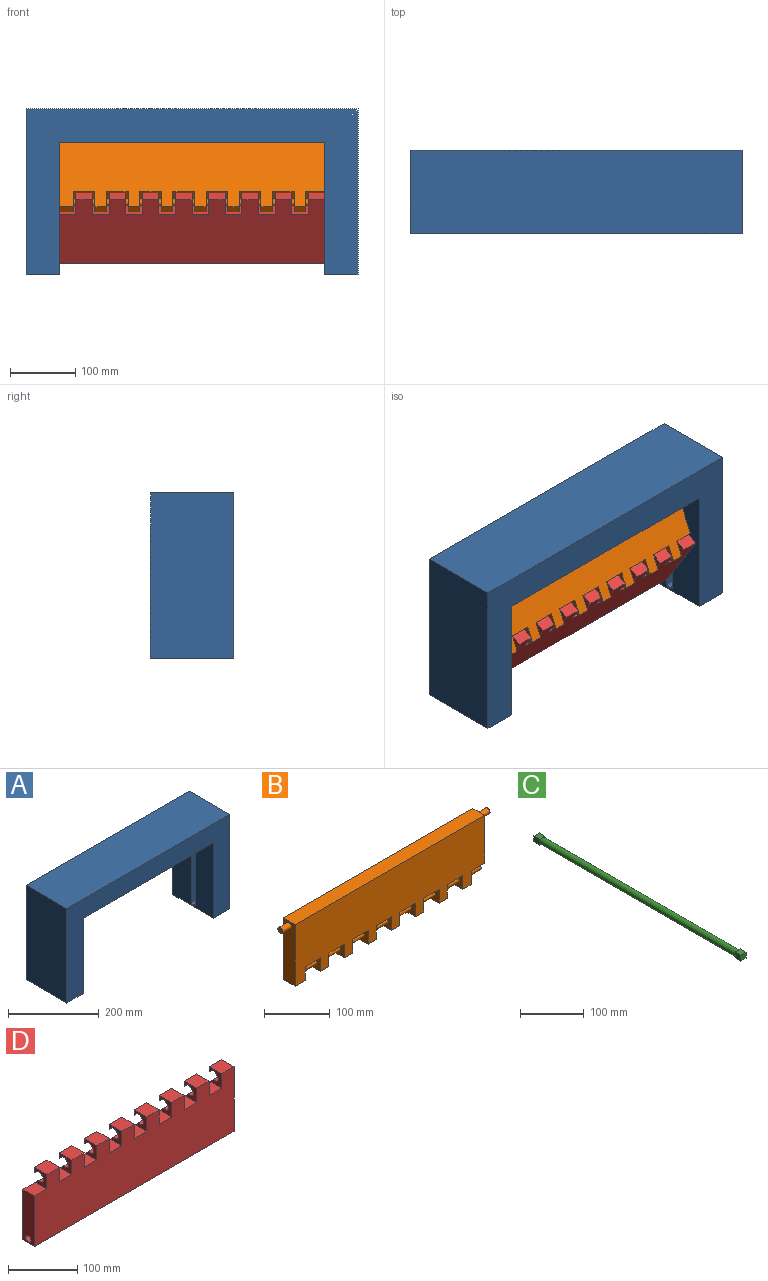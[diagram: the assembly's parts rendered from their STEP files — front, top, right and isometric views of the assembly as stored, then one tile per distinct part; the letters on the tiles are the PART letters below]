
ASSEMBLY  parts=4 mates=4
PART A: 32 faces, bbox 508x127x254 mm
  f0: plane 127x50.8mm, normal (0,0,-1), area 6451.6mm2, adj f1,f7,f8,f9
  f1: plane 203.2x127mm, normal (1,0,0), area 23379.3mm2, adj f0,f2,f8,f9,f12,f19,f21,f22
  f2: plane 406.4x127mm, normal (0,0,-1), area 51612.8mm2, adj f1,f3,f8,f9
  f3: plane 203.2x127mm, normal (-1,0,0), area 23379.3mm2, adj f2,f4,f8,f9,f11,f14,f15,f17
  f4: plane 127x50.8mm, normal (0,0,-1), area 6451.6mm2, adj f3,f5,f8,f9
  f5: plane 254x127mm, normal (1,0,0), area 32258mm2, adj f4,f6,f8,f9
  f6: plane 508x127mm, normal (0,0,1), area 64516mm2, adj f5,f7,f8,f9
  f7: plane 254x127mm, normal (-1,0,0), area 32258mm2, adj f0,f6,f8,f9
  f8: plane 508x254mm, normal (0,-1,0), area 46451.5mm2, adj f0,f1,f2,f3,f4,f5,f6,f7
  f9: plane 508x254mm, normal (0,1,0), area 46451.5mm2, adj f0,f1,f2,f3,f4,f5,f6,f7
  f10: plane 12.7x12.7mm, normal (-1,0,0), area 126.7mm2, adj f11
  f11: cylinder r=6.35mm len=25.4mm, axis (1,0,0), area 1013.4mm2, adj f3,f10
  f12: cylinder r=6.35mm len=25.4mm, axis (1,0,0), area 1013.4mm2, adj f1,f13
  f13: plane 12.7x12.7mm, normal (1,0,0), area 126.7mm2, adj f12
  f14: plane 25.4x2.54mm, normal (0,0,-1), area 64.5mm2, adj f3,f16,f29,f31
  f15: plane 25.4x2.54mm, normal (0,0,1), area 64.5mm2, adj f3,f16,f28,f30
  f16: plane 182.88x12.7mm, normal (-1,0,0), area 2300.4mm2, adj f14,f15,f17,f18,f28,f29,f30,f31
  f17: plane 172.72x25.4mm, normal (0,-1,0), area 4387.1mm2, adj f3,f16,f30,f31
  f18: plane 172.72x25.4mm, normal (0,1,0), area 4387.1mm2, adj f3,f16,f28,f29
  f19: plane 25.4x2.54mm, normal (0,0,-1), area 64.5mm2, adj f1,f20,f24,f26
  f20: plane 182.88x12.7mm, normal (1,0,0), area 2300.4mm2, adj f19,f21,f22,f23,f24,f25,f26,f27
  f21: plane 25.4x2.54mm, normal (0,0,1), area 64.5mm2, adj f1,f20,f25,f27
  f22: plane 172.72x25.4mm, normal (0,-1,0), area 4387.1mm2, adj f1,f20,f26,f27
  f23: plane 172.72x25.4mm, normal (0,1,0), area 4387.1mm2, adj f1,f20,f24,f25
  f24: cylinder r=5.08mm len=25.4mm, axis (1,0,0), area 202.7mm2, adj f1,f19,f20,f23
  f25: cylinder r=5.08mm len=25.4mm, axis (-1,0,0), area 202.7mm2, adj f1,f20,f21,f23
  f26: cylinder r=5.08mm len=25.4mm, axis (-1,0,0), area 202.7mm2, adj f1,f19,f20,f22
  f27: cylinder r=5.08mm len=25.4mm, axis (1,0,0), area 202.7mm2, adj f1,f20,f21,f22
  f28: cylinder r=5.08mm len=25.4mm, axis (-1,0,0), area 202.7mm2, adj f3,f15,f16,f18
  f29: cylinder r=5.08mm len=25.4mm, axis (1,0,0), area 202.7mm2, adj f3,f14,f16,f18
  f30: cylinder r=5.08mm len=25.4mm, axis (1,0,0), area 202.7mm2, adj f3,f15,f16,f17
  f31: cylinder r=5.08mm len=25.4mm, axis (-1,0,0), area 202.7mm2, adj f3,f14,f16,f17
PART B: 49 faces, bbox 444.5x25.4x114.3 mm
  f0: plane 29.21x25.4mm, normal (0,0,-1), area 741.9mm2, adj f1,f33,f34,f35
  f1: plane 88.9x25.4mm, normal (1,0,0), area 2177mm2, adj f0,f2,f34,f35,f47
  f2: plane 406.4x25.4mm, normal (0,0,1), area 10322.6mm2, adj f1,f3,f34,f35
  f3: plane 114.3x25.4mm, normal (-1,0,0), area 2822.1mm2, adj f2,f4,f34,f35,f46
  f4: plane 25.4x21.59mm, normal (0,0,-1), area 548.4mm2, adj f3,f5,f34,f35
  f5: plane 25.4x25.4mm, normal (1,0,0), area 564.1mm2, adj f4,f6,f34,f35,f44
  f6: plane 33.02x25.4mm, normal (0,0,-1), area 838.7mm2, adj f5,f7,f34,f35
  f7: plane 25.4x25.4mm, normal (-1,0,0), area 564.1mm2, adj f6,f8,f34,f35,f44
  f8: plane 25.4x17.78mm, normal (0,0,-1), area 451.6mm2, adj f7,f9,f34,f35
  f9: plane 25.4x25.4mm, normal (1,0,0), area 564.1mm2, adj f8,f10,f34,f35,f43
  f10: plane 33.02x25.4mm, normal (0,0,-1), area 838.7mm2, adj f9,f11,f34,f35
  f11: plane 25.4x25.4mm, normal (-1,0,0), area 564.1mm2, adj f10,f12,f34,f35,f43
  f12: plane 25.4x17.78mm, normal (0,0,-1), area 451.6mm2, adj f11,f13,f34,f35
  f13: plane 25.4x25.4mm, normal (1,0,0), area 564.1mm2, adj f12,f14,f34,f35,f42
  f14: plane 33.02x25.4mm, normal (0,0,-1), area 838.7mm2, adj f13,f15,f34,f35
  f15: plane 25.4x25.4mm, normal (-1,0,0), area 564.1mm2, adj f14,f16,f34,f35,f42
  f16: plane 25.4x17.78mm, normal (0,0,-1), area 451.6mm2, adj f15,f17,f34,f35
  f17: plane 25.4x25.4mm, normal (1,0,0), area 564.1mm2, adj f16,f18,f34,f35,f41
  f18: plane 33.02x25.4mm, normal (0,0,-1), area 838.7mm2, adj f17,f19,f34,f35
  f19: plane 25.4x25.4mm, normal (-1,0,0), area 564.1mm2, adj f18,f20,f34,f35,f41
  f20: plane 25.4x17.78mm, normal (0,0,-1), area 451.6mm2, adj f19,f21,f34,f35
  f21: plane 25.4x25.4mm, normal (1,0,0), area 564.1mm2, adj f20,f22,f34,f35,f40
  f22: plane 33.02x25.4mm, normal (0,0,-1), area 838.7mm2, adj f21,f23,f34,f35
  f23: plane 25.4x25.4mm, normal (-1,0,0), area 564.1mm2, adj f22,f24,f34,f35,f40
  f24: plane 25.4x17.78mm, normal (0,0,-1), area 451.6mm2, adj f23,f25,f34,f35
  f25: plane 25.4x25.4mm, normal (1,0,0), area 564.1mm2, adj f24,f26,f34,f35,f39
  f26: plane 33.02x25.4mm, normal (0,0,-1), area 838.7mm2, adj f25,f27,f34,f35
  f27: plane 25.4x25.4mm, normal (-1,0,0), area 564.1mm2, adj f26,f28,f34,f35,f39
  f28: plane 25.4x17.78mm, normal (0,0,-1), area 451.6mm2, adj f27,f29,f34,f35
  f29: plane 25.4x25.4mm, normal (1,0,0), area 564.1mm2, adj f28,f30,f34,f35,f38
  f30: plane 33.02x25.4mm, normal (0,0,-1), area 838.7mm2, adj f29,f31,f34,f35
  f31: plane 25.4x25.4mm, normal (-1,0,0), area 564.1mm2, adj f30,f32,f34,f35,f38
  f32: plane 25.4x17.78mm, normal (0,0,-1), area 451.6mm2, adj f31,f33,f34,f35
  f33: plane 25.4x25.4mm, normal (1,0,0), area 564.1mm2, adj f0,f32,f34,f35,f37
  f34: plane 406.4x114.3mm, normal (0,-1,0), area 39838.6mm2, adj f0,f1,f2,f3,f4,f5,f6,f7
  f35: plane 406.4x114.3mm, normal (0,1,0), area 39838.6mm2, adj f0,f1,f2,f3,f4,f5,f6,f7
  f36: plane 10.16x10.16mm, normal (1,0,0), area 81.1mm2, adj f37
  f37: cylinder r=5.08mm len=29.21mm, axis (-1,0,0), area 932.3mm2, adj f33,f36
  f38: cylinder r=5.08mm len=33.02mm, axis (-1,0,0), area 1054mm2, adj f29,f31
  f39: cylinder r=5.08mm len=33.02mm, axis (-1,0,0), area 1054mm2, adj f25,f27
  f40: cylinder r=5.08mm len=33.02mm, axis (-1,0,0), area 1054mm2, adj f21,f23
  f41: cylinder r=5.08mm len=33.02mm, axis (-1,0,0), area 1054mm2, adj f17,f19
  f42: cylinder r=5.08mm len=33.02mm, axis (-1,0,0), area 1054mm2, adj f13,f15
  f43: cylinder r=5.08mm len=33.02mm, axis (-1,0,0), area 1054mm2, adj f9,f11
  f44: cylinder r=5.08mm len=33.02mm, axis (-1,0,0), area 1054mm2, adj f5,f7
  f45: plane 10.16x10.16mm, normal (-1,0,0), area 81.1mm2, adj f46
  f46: cylinder r=5.08mm len=19.05mm, axis (1,0,0), area 608mm2, adj f3,f45
  f47: cylinder r=5.08mm len=19.05mm, axis (1,0,0), area 608mm2, adj f1,f48
  f48: plane 10.16x10.16mm, normal (1,0,0), area 81.1mm2, adj f47
PART C: 19 faces, bbox 11.4x457.2x11.4 mm
  f0: cylinder r=5.71mm len=431.8mm, axis (0,1,0), area 15505.2mm2, adj f5,f6,f7,f8,f14,f15,f16,f17
  f1: plane 12.7x11.43mm, normal (0,0,-1), area 145.2mm2, adj f2,f4,f5,f8,f9
  f2: plane 12.7x11.43mm, normal (1,0,0), area 145.2mm2, adj f1,f3,f5,f6,f9
  f3: plane 12.7x11.43mm, normal (0,0,1), area 145.2mm2, adj f2,f4,f6,f7,f9
  f4: plane 12.7x11.43mm, normal (-1,0,0), area 145.2mm2, adj f1,f3,f7,f8,f9
  f5: plane 5.72x5.72mm, normal (0,1,0), area 7mm2, adj f0,f1,f2
  f6: plane 5.72x5.72mm, normal (0,1,0), area 7mm2, adj f0,f2,f3
  f7: plane 5.72x5.72mm, normal (0,1,0), area 7mm2, adj f0,f3,f4
  f8: plane 5.72x5.72mm, normal (0,1,0), area 7mm2, adj f0,f1,f4
  f9: plane 11.43x11.43mm, normal (0,-1,0), area 130.6mm2, adj f1,f2,f3,f4
  f10: plane 12.7x11.43mm, normal (0,0,-1), area 145.2mm2, adj f11,f13,f15,f16,f18
  f11: plane 12.7x11.43mm, normal (-1,0,0), area 145.2mm2, adj f10,f12,f16,f17,f18
  f12: plane 12.7x11.43mm, normal (0,0,1), area 145.2mm2, adj f11,f13,f14,f17,f18
  f13: plane 12.7x11.43mm, normal (1,0,0), area 145.2mm2, adj f10,f12,f14,f15,f18
  f14: plane 5.72x5.72mm, normal (0,-1,0), area 7mm2, adj f0,f12,f13
  f15: plane 5.72x5.72mm, normal (0,-1,0), area 7mm2, adj f0,f10,f13
  f16: plane 5.72x5.72mm, normal (0,-1,0), area 7mm2, adj f0,f10,f11
  f17: plane 5.72x5.72mm, normal (0,-1,0), area 7mm2, adj f0,f11,f12
  f18: plane 11.43x11.43mm, normal (0,1,0), area 130.6mm2, adj f10,f11,f12,f13
PART D: 70 faces, bbox 406.4x25.4x114.3 mm
  f0: plane 25.4x25.4mm, normal (1,0,0), area 364.8mm2, adj f21,f23,f24,f42,f44,f51,f58,f59
  f1: plane 25.4x25.4mm, normal (-1,0,0), area 364.8mm2, adj f21,f24,f25,f42,f44,f51,f58,f59
  f2: plane 25.4x25.4mm, normal (1,0,0), area 364.8mm2, adj f20,f25,f26,f42,f45,f52,f58,f60
  f3: plane 25.4x25.4mm, normal (-1,0,0), area 364.8mm2, adj f20,f26,f27,f42,f45,f52,f58,f60
  f4: plane 25.4x25.4mm, normal (1,0,0), area 364.8mm2, adj f19,f27,f28,f42,f46,f53,f58,f61
  f5: plane 25.4x25.4mm, normal (-1,0,0), area 364.8mm2, adj f19,f28,f29,f42,f46,f53,f58,f61
  f6: plane 25.4x25.4mm, normal (1,0,0), area 364.8mm2, adj f18,f29,f30,f42,f47,f54,f58,f62
  f7: plane 25.4x25.4mm, normal (-1,0,0), area 364.8mm2, adj f18,f30,f31,f42,f47,f54,f58,f62
  f8: plane 25.4x25.4mm, normal (1,0,0), area 364.8mm2, adj f17,f31,f32,f42,f48,f55,f58,f63
  f9: plane 25.4x25.4mm, normal (-1,0,0), area 364.8mm2, adj f17,f32,f33,f42,f48,f55,f58,f63
  f10: plane 25.4x25.4mm, normal (1,0,0), area 364.8mm2, adj f16,f33,f34,f42,f49,f56,f58,f64
  f11: plane 25.4x25.4mm, normal (-1,0,0), area 364.8mm2, adj f16,f34,f35,f42,f49,f56,f58,f64
  f12: plane 25.4x25.4mm, normal (1,0,0), area 364.8mm2, adj f15,f35,f36,f42,f50,f57,f58,f65
  f13: plane 25.4x25.4mm, normal (-1,0,0), area 364.8mm2, adj f15,f36,f37,f42,f50,f57,f58,f65
  f14: plane 25.4x25.4mm, normal (-1,0,0), area 364.8mm2, adj f22,f23,f41,f42,f58,f66,f67,f68
  f15: plane 25.4x9.24mm, normal (0,1,0), area 234.6mm2, adj f12,f13,f36,f65
  f16: plane 25.4x9.24mm, normal (0,1,0), area 234.6mm2, adj f10,f11,f34,f64
  f17: plane 25.4x9.24mm, normal (0,1,0), area 234.6mm2, adj f8,f9,f32,f63
  f18: plane 25.4x9.24mm, normal (0,1,0), area 234.6mm2, adj f6,f7,f30,f62
  f19: plane 25.4x9.24mm, normal (0,1,0), area 234.6mm2, adj f4,f5,f28,f61
  f20: plane 25.4x9.24mm, normal (0,1,0), area 234.6mm2, adj f2,f3,f26,f60
  f21: plane 25.4x9.24mm, normal (0,1,0), area 234.6mm2, adj f0,f1,f24,f59
  f22: plane 25.4x9.24mm, normal (0,1,0), area 234.6mm2, adj f14,f40,f41,f66
  f23: plane 25.4x23.6mm, normal (0,0,1), area 599.5mm2, adj f0,f14,f42,f58
  f24: plane 25.4x25.4mm, normal (0,0,1), area 645.2mm2, adj f0,f1,f21,f42
  f25: plane 25.4x23.6mm, normal (0,0,1), area 599.5mm2, adj f1,f2,f42,f58
  f26: plane 25.4x25.4mm, normal (0,0,1), area 645.2mm2, adj f2,f3,f20,f42
  f27: plane 25.4x23.6mm, normal (0,0,1), area 599.5mm2, adj f3,f4,f42,f58
  f28: plane 25.4x25.4mm, normal (0,0,1), area 645.2mm2, adj f4,f5,f19,f42
  f29: plane 25.4x23.6mm, normal (0,0,1), area 599.5mm2, adj f5,f6,f42,f58
  f30: plane 25.4x25.4mm, normal (0,0,1), area 645.2mm2, adj f6,f7,f18,f42
  f31: plane 25.4x23.6mm, normal (0,0,1), area 599.5mm2, adj f7,f8,f42,f58
  f32: plane 25.4x25.4mm, normal (0,0,1), area 645.2mm2, adj f8,f9,f17,f42
  f33: plane 25.4x23.6mm, normal (0,0,1), area 599.5mm2, adj f9,f10,f42,f58
  f34: plane 25.4x25.4mm, normal (0,0,1), area 645.2mm2, adj f10,f11,f16,f42
  f35: plane 25.4x23.6mm, normal (0,0,1), area 599.5mm2, adj f11,f12,f42,f58
  f36: plane 25.4x25.4mm, normal (0,0,1), area 645.2mm2, adj f12,f13,f15,f42
  f37: plane 25.4x23.6mm, normal (0,0,1), area 599.5mm2, adj f13,f38,f42,f58
  f38: plane 88.9x25.4mm, normal (-1,0,0), area 2153.8mm2, adj f37,f39,f42,f43,f58,f69
  f39: plane 406.4x25.4mm, normal (0,0,-1), area 10322.6mm2, adj f38,f40,f42,f43
  f40: plane 114.3x25.4mm, normal (1,0,0), area 2518.7mm2, adj f22,f39,f41,f42,f43,f58,f66,f67
  f41: plane 25.4x25.4mm, normal (0,0,1), area 645.2mm2, adj f14,f22,f40,f42
  f42: plane 406.4x114.3mm, normal (0,-1,0), area 41290.2mm2, adj f0,f1,f2,f3,f4,f5,f6,f7
  f43: plane 406.4x87.1mm, normal (0,1,0), area 35399mm2, adj f38,f39,f40,f58
  f44: cylinder r=6.35mm len=25.4mm, axis (1,0,0), area 319.7mm2, adj f0,f1,f51,f59
  f45: cylinder r=6.35mm len=25.4mm, axis (1,0,0), area 319.7mm2, adj f2,f3,f52,f60
  f46: cylinder r=6.35mm len=25.4mm, axis (1,0,0), area 319.7mm2, adj f4,f5,f53,f61
  f47: cylinder r=6.35mm len=25.4mm, axis (1,0,0), area 319.7mm2, adj f6,f7,f54,f62
  f48: cylinder r=6.35mm len=25.4mm, axis (1,0,0), area 319.7mm2, adj f8,f9,f55,f63
  f49: cylinder r=6.35mm len=25.4mm, axis (1,0,0), area 319.7mm2, adj f10,f11,f56,f64
  f50: cylinder r=6.35mm len=25.4mm, axis (1,0,0), area 319.7mm2, adj f12,f13,f57,f65
  f51: cylinder r=6.35mm len=25.4mm, axis (1,0,0), area 540.6mm2, adj f0,f1,f44,f58
  f52: cylinder r=6.35mm len=25.4mm, axis (1,0,0), area 540.6mm2, adj f2,f3,f45,f58
  f53: cylinder r=6.35mm len=25.4mm, axis (1,0,0), area 540.6mm2, adj f4,f5,f46,f58
  f54: cylinder r=6.35mm len=25.4mm, axis (1,0,0), area 540.6mm2, adj f6,f7,f47,f58
  f55: cylinder r=6.35mm len=25.4mm, axis (1,0,0), area 540.6mm2, adj f8,f9,f48,f58
  f56: cylinder r=6.35mm len=25.4mm, axis (1,0,0), area 540.6mm2, adj f10,f11,f49,f58
  f57: cylinder r=6.35mm len=25.4mm, axis (1,0,0), area 540.6mm2, adj f12,f13,f50,f58
  f58: plane 406.4x9.2mm, normal (0,0.71,0.71), area 3159.5mm2, adj f0,f1,f2,f3,f4,f5,f6,f7
  f59: plane 25.4x4.62mm, normal (0,-0.71,-0.71), area 165.9mm2, adj f0,f1,f21,f44
  f60: plane 25.4x4.62mm, normal (0,-0.71,-0.71), area 165.9mm2, adj f2,f3,f20,f45
  f61: plane 25.4x4.62mm, normal (0,-0.71,-0.71), area 165.9mm2, adj f4,f5,f19,f46
  f62: plane 25.4x4.62mm, normal (0,-0.71,-0.71), area 165.9mm2, adj f6,f7,f18,f47
  f63: plane 25.4x4.62mm, normal (0,-0.71,-0.71), area 165.9mm2, adj f8,f9,f17,f48
  f64: plane 25.4x4.62mm, normal (0,-0.71,-0.71), area 165.9mm2, adj f10,f11,f16,f49
  f65: plane 25.4x4.62mm, normal (0,-0.71,-0.71), area 165.9mm2, adj f12,f13,f15,f50
  f66: plane 25.4x4.62mm, normal (0,-0.71,-0.71), area 165.9mm2, adj f14,f22,f40,f67
  f67: cylinder r=6.35mm len=25.4mm, axis (1,0,0), area 319.7mm2, adj f14,f40,f66,f68
  f68: cylinder r=6.35mm len=25.4mm, axis (1,0,0), area 540.6mm2, adj f14,f40,f58,f67
  f69: cylinder r=5.71mm len=406.4mm, axis (1,0,0), area 14593.2mm2, adj f38,f40
PLACE A t=(-143.82,-14.32,77.67)mm fixed
PLACE B rot(axis=(-1,0,0),23.7deg) t=(-143.82,-22.63,122.47)mm
PLACE C rot(axis=(0.71,-0.71,0),180deg) t=(-359.72,-2.26,7.24)mm
PLACE D rot(axis=(1,0,0),32.1deg) t=(-143.82,-17.79,55.96)mm
MATE revolute C.f0 <-> D.f69  axis (-1,0,0) through (84.78,-2.26,7.24)mm
MATE revolute B.f46 <-> A.f11  axis (1,0,0) through (78.43,-14.32,172.92)mm
MATE planar C.f13 <-> A.f22  axis (0,-1,0) through (-353.37,-7.97,7.24)mm
MATE revolute D.f51 <-> B.f37  axis (1,0,0) through (59.38,-52.15,86.89)mm
